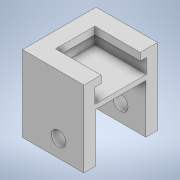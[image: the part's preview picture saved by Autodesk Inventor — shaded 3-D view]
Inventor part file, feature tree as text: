
AUTODESK INVENTOR PART (.ipt)
format: ipt  version: 2021.4 (Build 254397000, 397)  size: 152,064 bytes
history: native  units: mm
features: sketch x6, extrude x5, other x1, hole x1
ambient origin geometry x8: Origin, YZ Plane, XZ Plane, XY Plane, X Axis, Y Axis, Z Axis, Center Point
bodies: Body1 (feature_tree)
feature tree (13):
  other  "ソリッド1"
  extrude  "押し出し1"  Depth=25.0mm
  extrude  "押し出し2"  Depth=30.0mm
  hole  "穴1"  [1 undecoded]
  extrude  "押し出し5"  Depth=20.5mm
  extrude  "押し出し7"  Depth=20.5mm
  extrude  "押し出し8"  Depth=20.0mm TaperAngle=0.0deg
  sketch  "スケッチ1"
  sketch  "スケッチ2"
  sketch  "スケッチ4"
  sketch  "スケッチ6"
  sketch  "スケッチ8"
  sketch  "スケッチ9"
note: 1 required parameter value undecoded (feature->parameter linkage not recoverable at this tier; creation-order binding heuristic only, values carry confidence <= 0.55)
